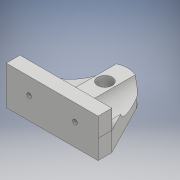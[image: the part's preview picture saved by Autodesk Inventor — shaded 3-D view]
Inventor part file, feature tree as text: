
AUTODESK INVENTOR PART (.ipt)
format: ipt  version: 2018.2 (Build 222227000, 227)  size: 151,040 bytes
history: native  units: mm
features: sketch x4, extrude x4
ambient origin geometry x8: Origin, YZ Plane, XZ Plane, XY Plane, X Axis, Y Axis, Z Axis, Center Point
bodies: Solid1 (feature_tree)
feature tree (8):
  sketch  "Sketch1"  dims[d9=4.2mm d10=0.0mm d11=4.2mm d12=0.0mm]
  extrude  "Extrusion1"  Depth=4.2mm TaperAngle=0.0deg
  extrude  "Extrusion2"  Depth=1.0mm
  extrude  "Extrusion3"  Depth=3.0mm
  extrude  "Extrusion4"  Depth=10.0mm
  sketch  "Sketch4"  dims[d13=1.0mm d14=1.0mm]
  sketch  "Sketch5"  dims[d15=5.5mm d16=0.0mm d17=3.0mm]
  sketch  "Sketch6"  dims[d18=3.0mm d19=11.5mm d23=90.0deg d24=90.0deg d25=10.0mm d31=5.0mm d32=120.0deg d33=14.0mm d34=6.0mm d35=6.0mm d36=10.0mm d37=0.0mm d38=4.8mm d39=4.8mm d40=4.8mm d41=4.8mm]
